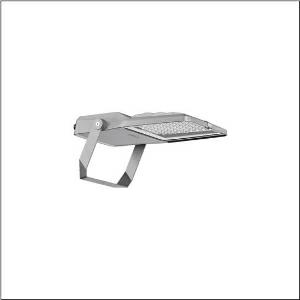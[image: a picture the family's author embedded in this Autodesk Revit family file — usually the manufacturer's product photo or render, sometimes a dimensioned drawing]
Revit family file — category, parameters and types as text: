
# Revit family: floodlight_fl_21_mini___pl43_5xa7776b2a1a_e86b
name_source: partatom
category: Lighting Fixtures
units: mm (PartAtom-declared; Revit-internal decimal feet)

## family parameters
Cut with Voids When Loaded = No
Host = Face
Light Source = No
Part Type = Normal
Room Calculation Point = No
Round Connector Dimension = Use Diameter
Shared = No

## types (1)
- --- (1 x LED, 6390 lm, 45.7 W, 3000K)
    Apparent Load = 46 VA
    CIE Flux Codes = 27 78 99 100 100
    Color Rendering = 70
    Color Temperature = 3000K
    Default Elevation = 1800 mm
    Description = Floodlight FL 21 mini, floodlight, primary light control with lens, of PMMA, primary optical cover: protective disc, of toughened safety glass, transparent, light distribution: PL43, light emission: direct distribution, installation type: surface-mounted, LED, High Power LED, rated luminous flux: 6.390lm, luminous efficacy: 140lm/W, light colour: 730, colour temperature: 3000K, control gear: Smart Interface (Zhaga), control: flexible luminous flux parameterisation, time-dependent luminous flux control, constant luminous flux control, overheat protection, pre-setting: logarithmic dimming characteristic, with terminal, 6-pole, mains connection: 220..240V, AC, 50/60Hz, start of lifetime: 46W, end of service life: 48W, reduction: 22W, luminaire housing, of diecast aluminium, powder-coated, SITECO metallic grey (DB 702S), corrosivity category C5 mid according to DIN EN ISO 12944, suitable for swimming pools, chlorine-resistant, sealing non-destructively replaceable, mounting bracket, of steel, galvanised, powder-coated, SITECO metallic grey (DB 702S), Smart Interface below and above, protection rating (complete): IP66, insulation class (complete): insulation class II (safety insulation), certification: CE, ENEC, VDE, protection symbol: D, impact resistance: IK08, permissible operating ambient temperature: -40..+40°C, permissible operating ambient temperature for outdoor applications: -40..+50°C, standard: DIN EN 12944, LABS conformity tested according to VDMA 24364:2018-05, packaging unit: 1 piece

Light Distribution: PL43
    Height = 70 mm
    Lamp = 1 x LED
    Lamp Light Flux = 6390 lm
    Lamp Power = 45.7 W
    Lamp count = 1
    Length = 485 mm
    Luminous efficacy = 140 lm/W
    Manufacturer = Siteco
    ModVariant = No
    Model = 5XA7776B2A1A
    Number of Poles = 1
    OnlyDefault = Yes
    Power Factor = 1
    Product Name = Floodlight FL 21 mini | PL43
    Product group = floodlight | pylon annexe
    ProductGroupID = 6201
    Protection Class = Protection class II
    Protection Degree = IP 66
    RLX_Detail_Level = 1
    RLX_Emergency_Light_Flux = 0 lm
    RLX_Emergency_Type = 0
    RLX_Emergency_Type_DB = No
    RlxData = <blob elided: 96013 chars, md5=a6d9959e>
    Socket = socket
    Standby Power = 0 W
    System Light Flux = 6390 lm
    System Power = 46 W
    Type Comments = factory setting: luminous flux: 100 % | dim-lin: 254 | 463 mA
    Type Image = l_1006845.jpg
    URL = http://relux.com
    VarID = @adj_160753
    Voltage = 0 V
    Weight = 0.00 kg
    Width = 337 mm

## geometry (parser evidence)
native form markers: Blend x4, Sweep x11
no freeform markers — native parametric forms only
